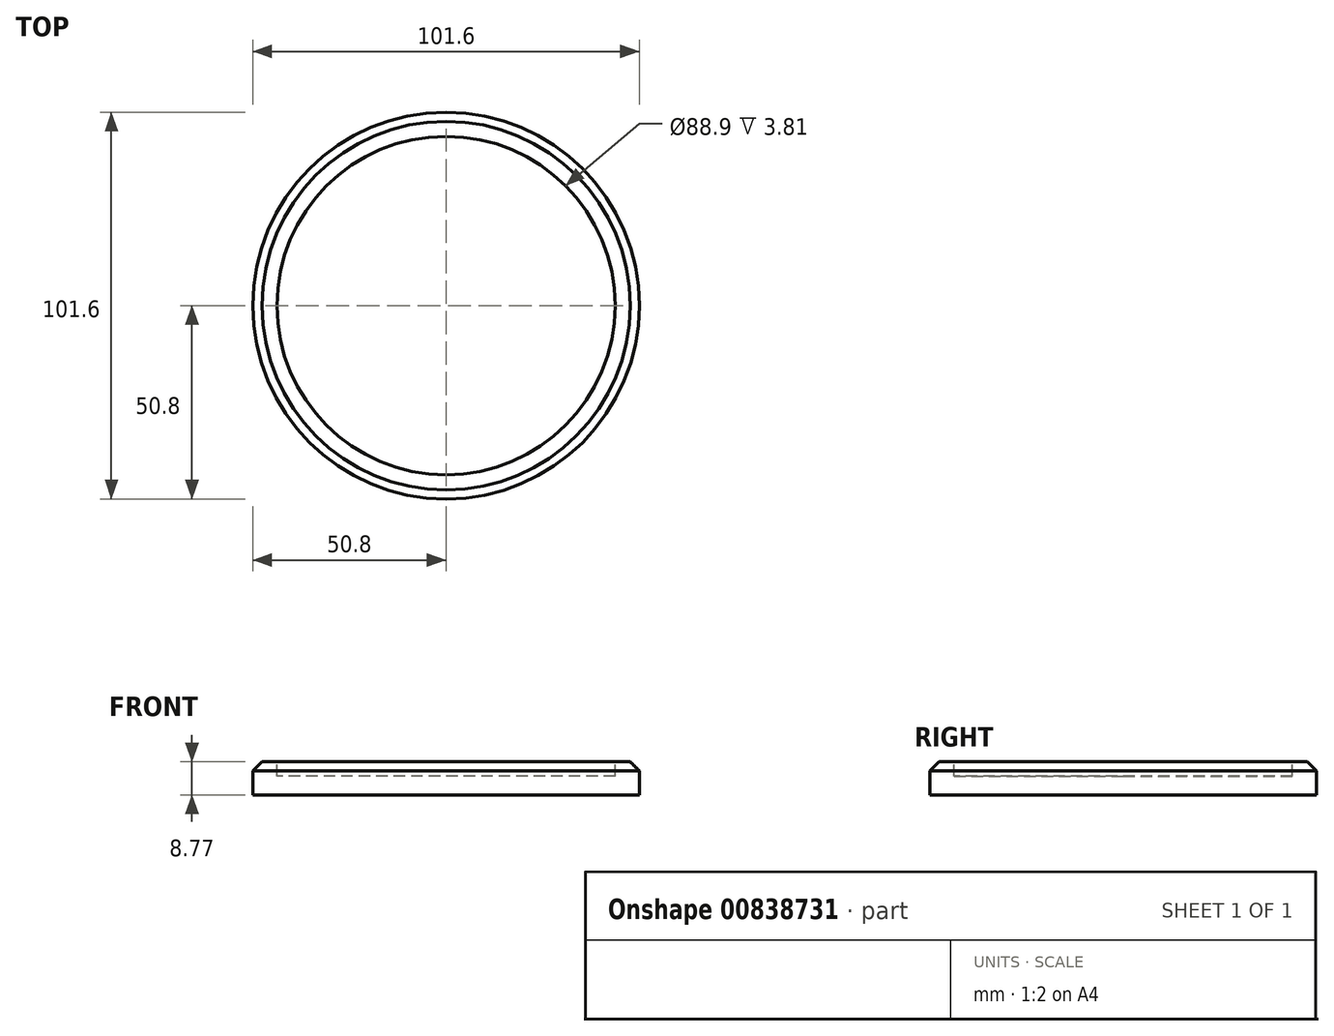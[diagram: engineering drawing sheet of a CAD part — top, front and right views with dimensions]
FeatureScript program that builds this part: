
annotation { "Feature Type Name" : "Feature", "Feature Type Description" : "" }
export const myFeature = defineFeature(function(context is Context, id is Id, definition is map)
    precondition{}
    {
        {
            var Q0;
            Q0=qCreatedBy(makeId("Front.planeOp"),FACE);
            var sketch = newSketch(context, id + "F0", { "sketchPlane" : qUnion([Q0])});
            skLineSegment(sketch, "E0", {"start": v(0, 0) * mm, "end": v(-50.8, 0) * mm});
            skLineSegment(sketch, "E1", {"start": v(-50.8, 0) * mm, "end": v(-50.8, 6.35) * mm});
            skLineSegment(sketch, "E2", {"start": v(-50.8, 6.35) * mm, "end": v(-48.38, 8.77) * mm});
            skLineSegment(sketch, "E3", {"start": v(-48.38, 8.77) * mm, "end": v(-44.45, 8.77) * mm});
            skLineSegment(sketch, "E4", {"start": v(-44.45, 8.77) * mm, "end": v(-44.45, 4.96) * mm});
            skLineSegment(sketch, "E5", {"start": v(-44.45, 4.96) * mm, "end": v(0, 4.96) * mm});
            skLineSegment(sketch, "E6", {"start": v(0, 4.96) * mm, "end": v(0, 0) * mm});
            skSolve(sketch);
        }
        {
            var Q0;
            Q0 = qSketchRegion(id + "F0", true);
            var Q1;
            Q1=sQuery(id+"F0.wireOp",EDGE,"E6");
            revolve(context, id + "F1", {"surfaceOperationType" : NewSurfaceOperationType.NEW, "entities" : qUnion([Q0]), "axis" : qUnion([Q1]), "revolveType" : RevolveType.FULL});
        }
    });
